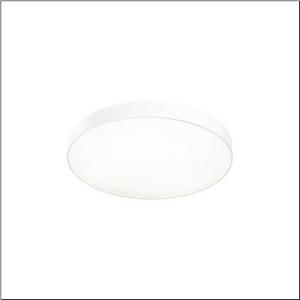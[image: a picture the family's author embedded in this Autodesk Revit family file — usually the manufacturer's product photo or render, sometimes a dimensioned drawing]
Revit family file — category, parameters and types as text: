
# Revit family: round_21_m_51mr36gm8321w
name_source: partatom
category: Lighting Fixtures
units: mm (PartAtom-declared; Revit-internal decimal feet)

## family parameters
Cut with Voids When Loaded = No
Host = Face
Light Source = No
Part Type = Normal
Room Calculation Point = No
Round Connector Dimension = Use Diameter
Shared = No

## types (1)
- --- (1 x LED, 8610 lm, 62.3 W, 3000K)
    Apparent Load = 62 VA
    CIE Flux Codes = 49 80 96 85 100
    Color Rendering = 80
    Color Temperature = 3000K
    Default Elevation = 1800 mm
    Description = Round 21 M, wall and ceiling luminaire, primary optical cover: cover, of PMMA, opal, light emission: direct/indirect distribution, primary light characteristic: symmetric, installation type: suspended mounting, surface-mounted, LED, rated luminous flux: 8.600lm, luminous efficacy: 138lm/W, light colour: 830, colour temperature: 3000K, control gear: ON/OFF Multilumen, with terminal, 3-pole, mains connection: 230V, AC, 50/60Hz, rated input power: 62.3W, housing, of aluminium, coated, white, diameter: 600mm, height: 62mm, protection rating (complete): IP40, insulation class (complete): insulation class I (protective earthing), certification: CE, impact resistance: IK04, permissible operating ambient temperature: -10..+35°C, packaging unit: 1 piece
    Height = 87 mm
    Lamp = 1 x LED
    Lamp Light Flux = 8610 lm
    Lamp Power = 62.3 W
    Lamp count = 1
    Length = 600 mm
    Luminous efficacy = 138 lm/W
    Manufacturer = Siteco
    ModVariant = No
    Model = 51MR36GM8321W
    Mounting Place = Ceiling
    Mounting Type = Surface mounted
    Number of Poles = 1
    OnlyDefault = Yes
    Power Factor = 1
    Product Name = Round 21 M
    Product group = wall and ceiling luminaire | ceiling mounted
    ProductGroupID = 304
    Protection Class = Protection class I
    Protection Degree = IP 40
    RLX_Detail_Level = 1
    RLX_Emergency_Light_Flux = 0 lm
    RLX_Emergency_Type = 0
    RLX_Emergency_Type_DB = No
    RlxData = <blob elided: 14833 chars, md5=30629fe7>
    Socket = socket
    Standby Power = 0 W
    System Light Flux = 8610 lm
    System Power = 62 W
    Type Comments = factory setting: luminous flux: 100 % | (ON | ON | ON | ON) | 700 mA
    Type Image = l_1258330.jpg
    URL = http://relux.com
    VarID = @adj_039321
    Voltage = 0 V
    Weight = 0.00 kg
    Width = 0 mm  [stored 0 ft]

note: [stored X ft] marks values corroborated as IEEE doubles in the binary element streams (Revit-internal decimal feet)

## geometry (parser evidence)
native form markers: Sweep x14
no freeform markers — native parametric forms only
